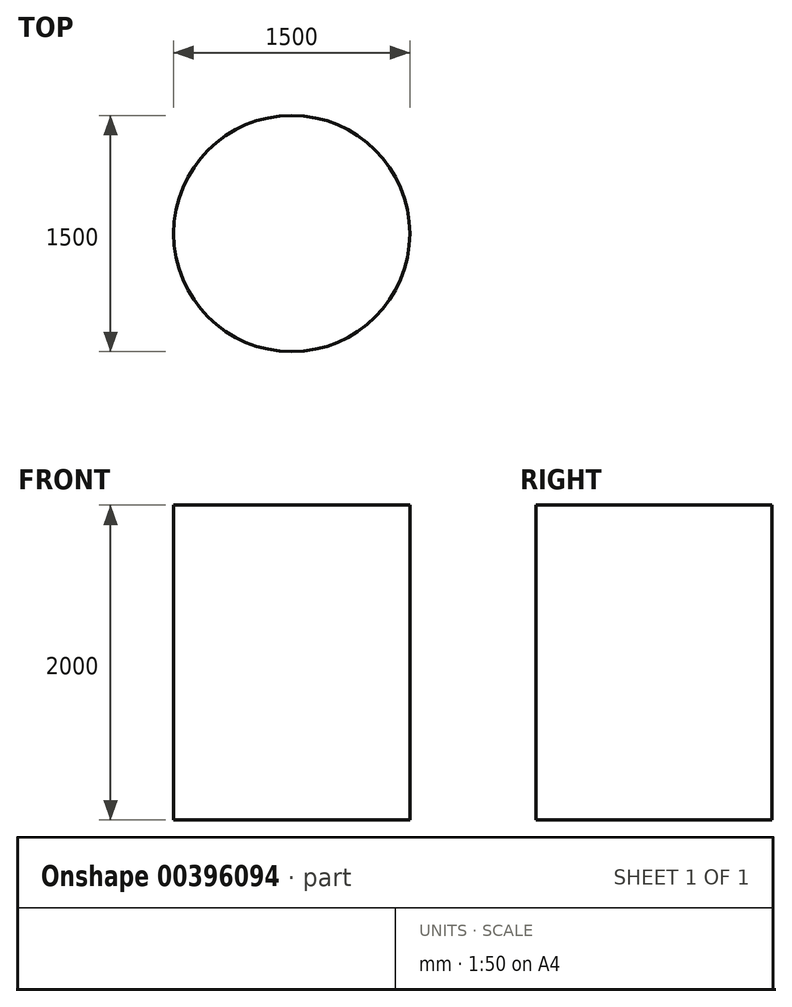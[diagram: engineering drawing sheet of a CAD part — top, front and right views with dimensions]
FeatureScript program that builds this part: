
annotation { "Feature Type Name" : "Feature", "Feature Type Description" : "" }
export const myFeature = defineFeature(function(context is Context, id is Id, definition is map)
    precondition{}
    {
        {
            var Q0;
            Q0=qCreatedBy(makeId("Top.planeOp"),FACE);
            var sketch = newSketch(context, id + "F0", { "sketchPlane" : qUnion([Q0])});
            skCircle(sketch, "E0", {"center": v(0, 0) * mm, "radius": 750 * mm});
            skSolve(sketch);
        }
        {
            var Q0;
            Q0 = qSketchRegion(id + "F0", true);
            extrude(context, id + "F1", {"entities" : qUnion([Q0]), "depth" : 2000 * mm, "offsetDistance" : 25 * mm});
        }
    });
